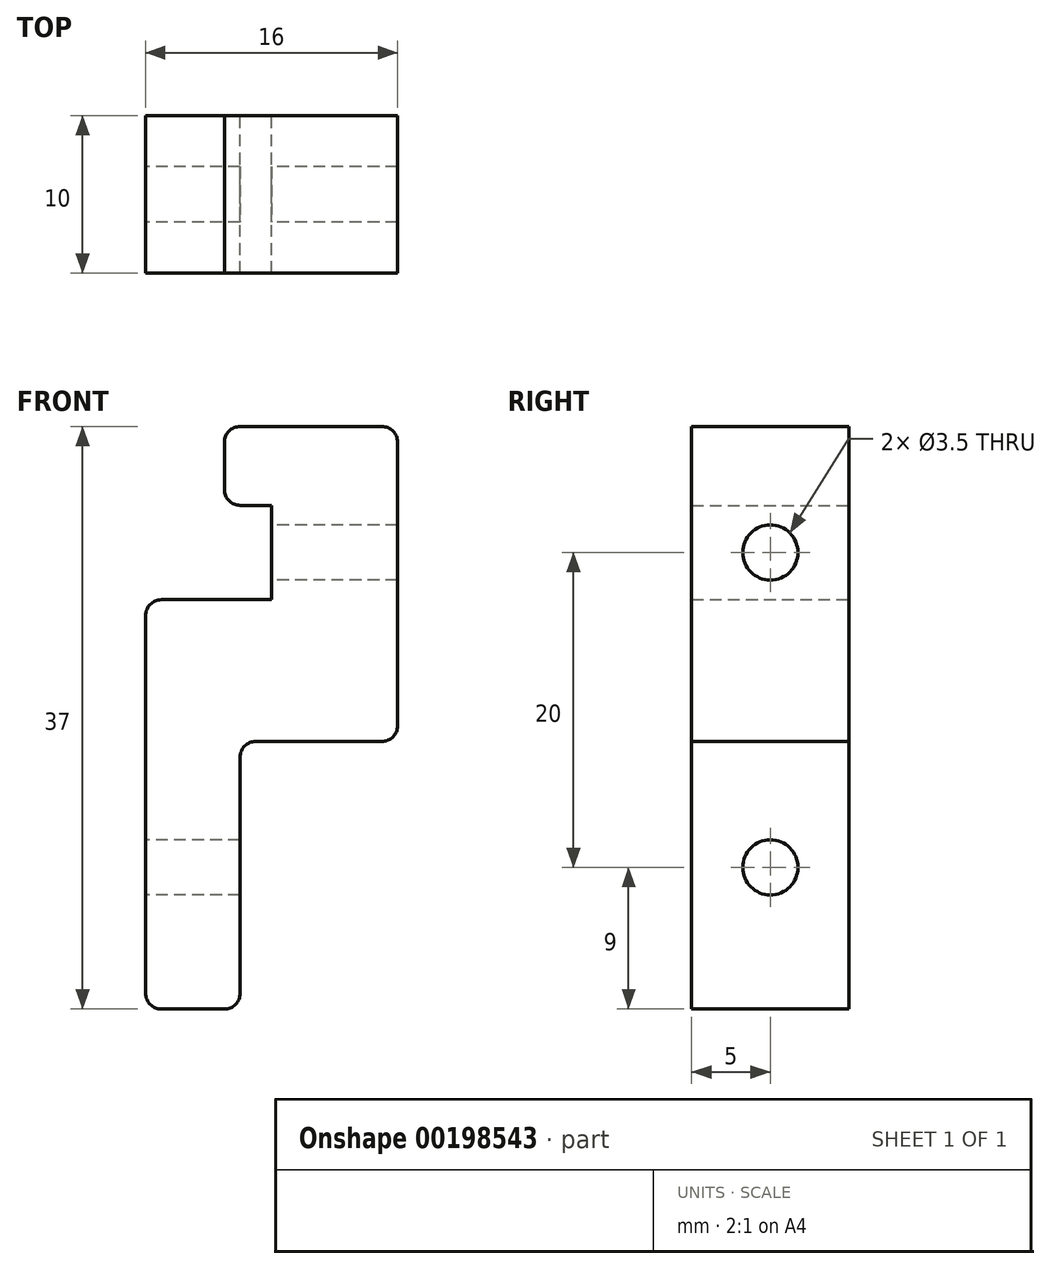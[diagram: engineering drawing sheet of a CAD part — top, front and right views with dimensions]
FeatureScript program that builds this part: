
annotation { "Feature Type Name" : "Feature", "Feature Type Description" : "" }
export const myFeature = defineFeature(function(context is Context, id is Id, definition is map)
    precondition{}
    {
        {
            var Q0;
            Q0=qCreatedBy(makeId("Front.planeOp"),FACE);
            var sketch = newSketch(context, id + "F0", { "sketchPlane" : qUnion([Q0])});
            skLineSegment(sketch, "E0", {"start": v(0, 0) * mm, "end": v(0, 20) * mm});
            skLineSegment(sketch, "E1", {"start": v(0, 20) * mm, "end": v(-11, 20) * mm});
            skLineSegment(sketch, "E2", {"start": v(-11, 20) * mm, "end": v(-11, 15) * mm});
            skLineSegment(sketch, "E3", {"start": v(-11, 15) * mm, "end": v(-8, 15) * mm});
            skLineSegment(sketch, "E4", {"start": v(-8, 15) * mm, "end": v(-8, 9) * mm});
            skLineSegment(sketch, "E5", {"start": v(-8, 9) * mm, "end": v(-16, 9) * mm});
            skLineSegment(sketch, "E6", {"start": v(-16, 9) * mm, "end": v(-16, -17) * mm});
            skLineSegment(sketch, "E7", {"start": v(-16, -17) * mm, "end": v(-10, -17) * mm});
            skLineSegment(sketch, "E8", {"start": v(-10, -17) * mm, "end": v(-10, 0) * mm});
            skLineSegment(sketch, "E9", {"start": v(-10, 0) * mm, "end": v(0, 0) * mm});
            skSolve(sketch);
        }
        {
            var Q0;
            Q0 = qSketchRegion(id + "F0", true);
            extrude(context, id + "F1", {"entities" : qUnion([Q0]), "depth" : 10 * mm});
        }
        {
            var Q0;
            Q0=makeQuery(id+"F1.opExtrude","SWEPT_FACE",FACE,{"disambiguationData":[OSD([sQuery(id+"F0.wireOp",EDGE,"E4")])]});
            var sketch = newSketch(context, id + "F2", { "sketchPlane" : qUnion([Q0])});
            skPoint(sketch, "E10", {"position": v(5, 12) * mm});
            skSolve(sketch);
        }
        {
            var Q0;
            Q0=sQuery(id+"F2.wireOp",VERTEX,"E10");
            var Q1;
            Q1=makeQuery(id+"F1.opExtrude","SWEPT_BODY",BODY,{"disambiguationData":[OSD([sQuery(id+"F0.wireOp",EDGE,"E0"),sQuery(id+"F0.wireOp",EDGE,"E1"),sQuery(id+"F0.wireOp",EDGE,"E2"),sQuery(id+"F0.wireOp",EDGE,"E3"),sQuery(id+"F0.wireOp",EDGE,"E4"),sQuery(id+"F0.wireOp",EDGE,"E5"),sQuery(id+"F0.wireOp",EDGE,"E6"),sQuery(id+"F0.wireOp",EDGE,"E7"),sQuery(id+"F0.wireOp",EDGE,"E8"),sQuery(id+"F0.wireOp",EDGE,"E9")])]});
            hole(context, id + "F3", {"style" : HoleStyle.SIMPLE, "endStyle" : HoleEndStyle.THROUGH, "holeDiameter" : 3.5 * mm, "locations" : qUnion([Q0]), "scope" : qUnion([Q1]), "isTappedThrough" : true});
        }
        {
            var Q0;
            Q0=makeQuery(id+"F1.opExtrude","SWEPT_EDGE",EDGE,{"disambiguationData":[OSD([sQuery(id+"F0.wireOp",EDGE,"E1"),sQuery(id+"F0.wireOp",EDGE,"E2")])]});
            var Q1;
            Q1=makeQuery(id+"F1.opExtrude","SWEPT_EDGE",EDGE,{"disambiguationData":[OSD([sQuery(id+"F0.wireOp",EDGE,"E2"),sQuery(id+"F0.wireOp",EDGE,"E3")])]});
            var Q2;
            Q2=makeQuery(id+"F1.opExtrude","SWEPT_EDGE",EDGE,{"disambiguationData":[OSD([sQuery(id+"F0.wireOp",EDGE,"E5"),sQuery(id+"F0.wireOp",EDGE,"E6")])]});
            var Q3;
            Q3=makeQuery(id+"F1.opExtrude","SWEPT_EDGE",EDGE,{"disambiguationData":[OSD([sQuery(id+"F0.wireOp",EDGE,"E6"),sQuery(id+"F0.wireOp",EDGE,"E7")])]});
            var Q4;
            Q4=makeQuery(id+"F1.opExtrude","SWEPT_EDGE",EDGE,{"disambiguationData":[OSD([sQuery(id+"F0.wireOp",EDGE,"E7"),sQuery(id+"F0.wireOp",EDGE,"E8")])]});
            var Q5;
            Q5=makeQuery(id+"F1.opExtrude","SWEPT_EDGE",EDGE,{"disambiguationData":[OSD([sQuery(id+"F0.wireOp",EDGE,"E8"),sQuery(id+"F0.wireOp",EDGE,"E9")])]});
            var Q6;
            Q6=makeQuery(id+"F1.opExtrude","SWEPT_EDGE",EDGE,{"disambiguationData":[OSD([sQuery(id+"F0.wireOp",EDGE,"E0"),sQuery(id+"F0.wireOp",EDGE,"E9")])]});
            var Q7;
            Q7=makeQuery(id+"F1.opExtrude","SWEPT_EDGE",EDGE,{"disambiguationData":[OSD([sQuery(id+"F0.wireOp",EDGE,"E0"),sQuery(id+"F0.wireOp",EDGE,"E1")])]});
            fillet(context, id + "F4", {"entities" : qUnion([Q0, Q1, Q2, Q3, Q4, Q5, Q6, Q7]), "radius" : 1 * mm, "tangentPropagation" : true, "allowEdgeOverflow" : false});
        }
        {
            var Q0;
            Q0=makeQuery(id+"F1.opExtrude","SWEPT_FACE",FACE,{"disambiguationData":[OSD([sQuery(id+"F0.wireOp",EDGE,"E6")])]});
            var sketch = newSketch(context, id + "F5", { "sketchPlane" : qUnion([Q0])});
            skPoint(sketch, "E11", {"position": v(5, -8) * mm});
            skSolve(sketch);
        }
        {
            var Q0;
            Q0=sQuery(id+"F5.wireOp",VERTEX,"E11");
            var Q1;
            Q1=makeQuery(id+"F1.opExtrude","SWEPT_BODY",BODY,{"disambiguationData":[OSD([sQuery(id+"F0.wireOp",EDGE,"E0"),sQuery(id+"F0.wireOp",EDGE,"E1"),sQuery(id+"F0.wireOp",EDGE,"E2"),sQuery(id+"F0.wireOp",EDGE,"E3"),sQuery(id+"F0.wireOp",EDGE,"E4"),sQuery(id+"F0.wireOp",EDGE,"E5"),sQuery(id+"F0.wireOp",EDGE,"E6"),sQuery(id+"F0.wireOp",EDGE,"E7"),sQuery(id+"F0.wireOp",EDGE,"E8"),sQuery(id+"F0.wireOp",EDGE,"E9")])]});
            hole(context, id + "F6", {"style" : HoleStyle.SIMPLE, "endStyle" : HoleEndStyle.THROUGH, "holeDiameter" : 3.5 * mm, "locations" : qUnion([Q0]), "scope" : qUnion([Q1]), "isTappedThrough" : true});
        }
    });
